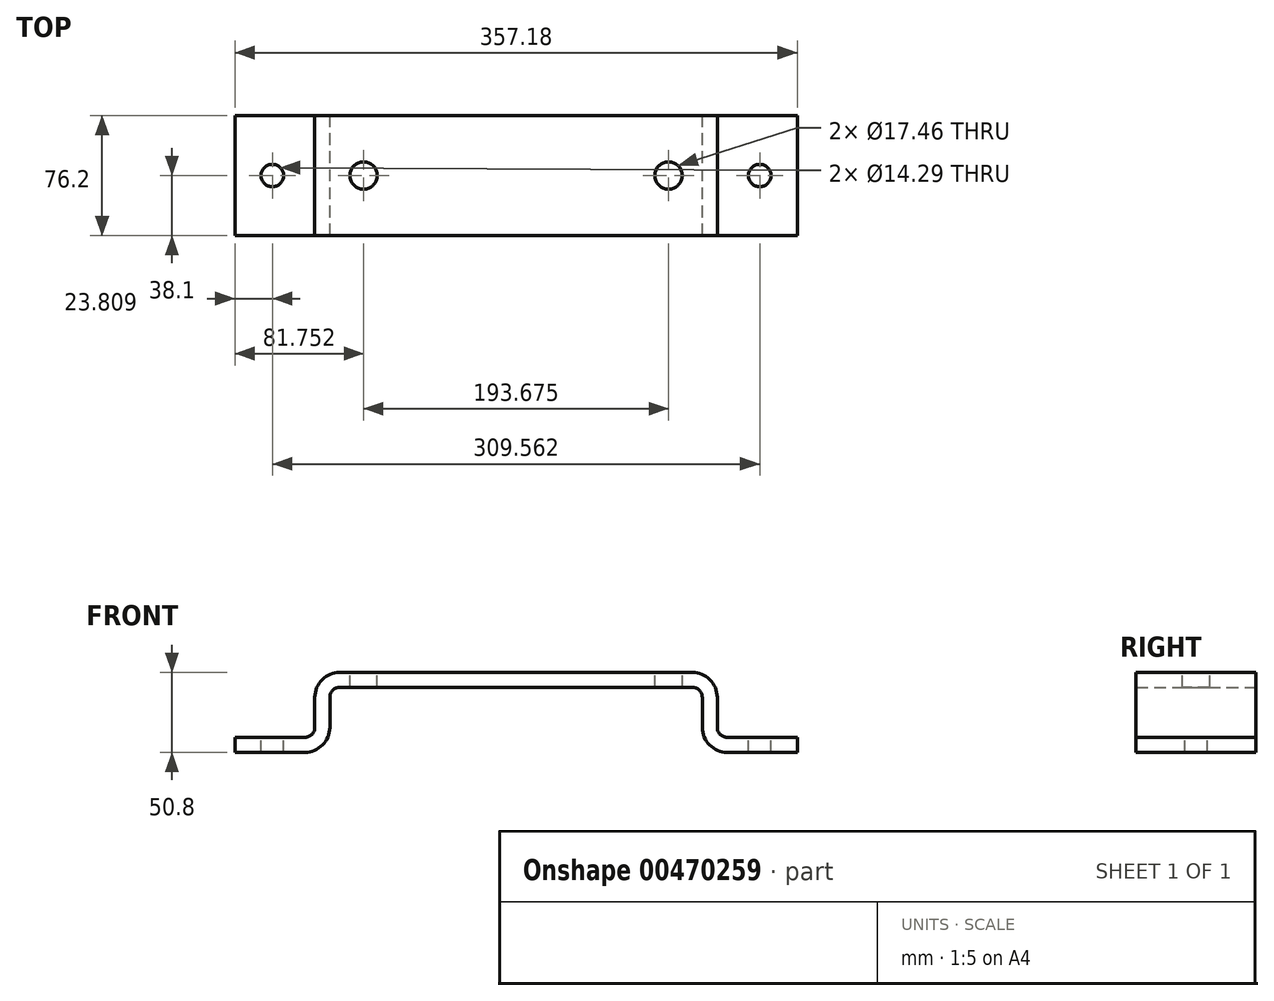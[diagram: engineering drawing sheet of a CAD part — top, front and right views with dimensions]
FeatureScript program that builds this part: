
annotation { "Feature Type Name" : "Feature", "Feature Type Description" : "" }
export const myFeature = defineFeature(function(context is Context, id is Id, definition is map)
    precondition{}
    {
        {
            var Q0;
            Q0=qCreatedBy(makeId("Front.planeOp"),FACE);
            var sketch = newSketch(context, id + "F0", { "sketchPlane" : qUnion([Q0])});
            skLineSegment(sketch, "E0.bottom", {"start": v(-178.6, -25.4) * mm, "end": v(-118.27, -25.4) * mm});
            skLineSegment(sketch, "E0.top", {"start": v(-127.8, 25.4) * mm, "end": v(127.8, 25.4) * mm});
            skLineSegment(sketch, "E0.left", {"start": v(-178.6, -25.4) * mm, "end": v(-178.6, -15.88) * mm});
            skLineSegment(sketch, "E0.right", {"start": v(178.6, -25.4) * mm, "end": v(178.6, -15.88) * mm});
            skPoint(sketch, "E0.middle", {"position": v(0, 0) * mm});
            skLineSegment(sketch, "E1.0", {"start": v(-178.6, -15.88) * mm, "end": v(-127.8, -15.88) * mm});
            skLineSegment(sketch, "E2.0", {"start": v(127.8, -15.88) * mm, "end": v(127.8, 25.4) * mm});
            skLineSegment(sketch, "E3.0", {"start": v(118.27, -25.4) * mm, "end": v(118.27, 15.88) * mm});
            skLineSegment(sketch, "E4.0", {"start": v(-127.8, -15.88) * mm, "end": v(-127.8, 25.4) * mm});
            skLineSegment(sketch, "E5.0", {"start": v(-118.27, -25.4) * mm, "end": v(-118.27, 15.87) * mm});
            skLineSegment(sketch, "E6.0", {"start": v(-118.27, 15.88) * mm, "end": v(118.27, 15.88) * mm});
            skPoint(sketch, "E7.orphan", {"position": v(-178.6, 25.4) * mm});
            skLineSegment(sketch, "E8.trimOffspring", {"start": v(127.8, -15.88) * mm, "end": v(178.6, -15.88) * mm});
            skLineSegment(sketch, "E9.trimOffspring", {"start": v(118.27, -25.4) * mm, "end": v(178.6, -25.4) * mm});
            skPoint(sketch, "E10.orphan", {"position": v(178.6, 25.4) * mm});
            skSolve(sketch);
        }
        {
            var Q0;
            Q0 = qSketchRegion(id + "F0", true);
            extrude(context, id + "F1", {"entities" : qUnion([Q0]), "endBound" : BoundingType.SYMMETRIC, "depth" : 76.2 * mm});
        }
        {
            var Q0;
            Q0=makeQuery(id+"F1.opExtrude","SWEPT_EDGE",EDGE,{"disambiguationData":[OSD([sQuery(id+"F0.wireOp",EDGE,"E1.0"),sQuery(id+"F0.wireOp",EDGE,"E4.0")])]});
            var Q1;
            Q1=makeQuery(id+"F1.opExtrude","SWEPT_EDGE",EDGE,{"disambiguationData":[OSD([sQuery(id+"F0.wireOp",EDGE,"E5.0"),sQuery(id+"F0.wireOp",EDGE,"E6.0")])]});
            var Q2;
            Q2=makeQuery(id+"F1.opExtrude","SWEPT_EDGE",EDGE,{"disambiguationData":[OSD([sQuery(id+"F0.wireOp",EDGE,"E3.0"),sQuery(id+"F0.wireOp",EDGE,"E6.0")])]});
            var Q3;
            Q3=makeQuery(id+"F1.opExtrude","SWEPT_EDGE",EDGE,{"disambiguationData":[OSD([sQuery(id+"F0.wireOp",EDGE,"E2.0"),sQuery(id+"F0.wireOp",EDGE,"E8.trimOffspring")])]});
            fillet(context, id + "F2", {"entities" : qUnion([Q0, Q1, Q2, Q3]), "radius" : 6.35 * mm, "tangentPropagation" : true, "allowEdgeOverflow" : false});
        }
        {
            var Q0;
            Q0=makeQuery(id+"F1.opExtrude","SWEPT_EDGE",EDGE,{"disambiguationData":[OSD([sQuery(id+"F0.wireOp",EDGE,"E0.top"),sQuery(id+"F0.wireOp",EDGE,"E4.0")])]});
            var Q1;
            Q1=makeQuery(id+"F1.opExtrude","SWEPT_EDGE",EDGE,{"disambiguationData":[OSD([sQuery(id+"F0.wireOp",EDGE,"E0.top"),sQuery(id+"F0.wireOp",EDGE,"E2.0")])]});
            var Q2;
            Q2=makeQuery(id+"F1.opExtrude","SWEPT_EDGE",EDGE,{"disambiguationData":[OSD([sQuery(id+"F0.wireOp",EDGE,"E3.0"),sQuery(id+"F0.wireOp",EDGE,"E9.trimOffspring")])]});
            var Q3;
            Q3=makeQuery(id+"F1.opExtrude","SWEPT_EDGE",EDGE,{"disambiguationData":[OSD([sQuery(id+"F0.wireOp",EDGE,"E0.bottom"),sQuery(id+"F0.wireOp",EDGE,"E5.0")])]});
            fillet(context, id + "F3", {"entities" : qUnion([Q0, Q1, Q2, Q3]), "radius" : 15.88 * mm, "tangentPropagation" : true, "allowEdgeOverflow" : false});
        }
        {
            var Q0;
            Q0=makeQuery(id+"F1.opExtrude","SWEPT_FACE",FACE,{"disambiguationData":[OSD([sQuery(id+"F0.wireOp",EDGE,"E0.top")])]});
            var sketch = newSketch(context, id + "F4", { "sketchPlane" : qUnion([Q0])});
            skCircle(sketch, "E11", {"center": v(-96.84, 0) * mm, "radius": 8.73 * mm});
            skCircle(sketch, "E12.MirrorC", {"center": v(96.84, 0) * mm, "radius": 8.73 * mm});
            skSolve(sketch);
        }
        {
            var Q0;
            Q0 = qSketchRegion(id + "F4", true);
            extrude(context, id + "F5", {"entities" : qUnion([Q0]), "operationType" : NewBodyOperationType.REMOVE, "oppositeDirection" : true, "depth" : 25.4 * mm});
        }
        {
            var Q0;
            Q0=makeQuery(id+"F1.opExtrude","SWEPT_FACE",FACE,{"disambiguationData":[OSD([sQuery(id+"F0.wireOp",EDGE,"E1.0")])]});
            var sketch = newSketch(context, id + "F6", { "sketchPlane" : qUnion([Q0])});
            skCircle(sketch, "E13", {"center": v(-154.78, 0) * mm, "radius": 7.14 * mm});
            skCircle(sketch, "E14.MirrorC", {"center": v(154.78, 0) * mm, "radius": 7.14 * mm});
            skSolve(sketch);
        }
        {
            var Q0;
            Q0 = qSketchRegion(id + "F6", true);
            extrude(context, id + "F7", {"entities" : qUnion([Q0]), "operationType" : NewBodyOperationType.REMOVE, "oppositeDirection" : true, "depth" : 25.4 * mm});
        }
    });
